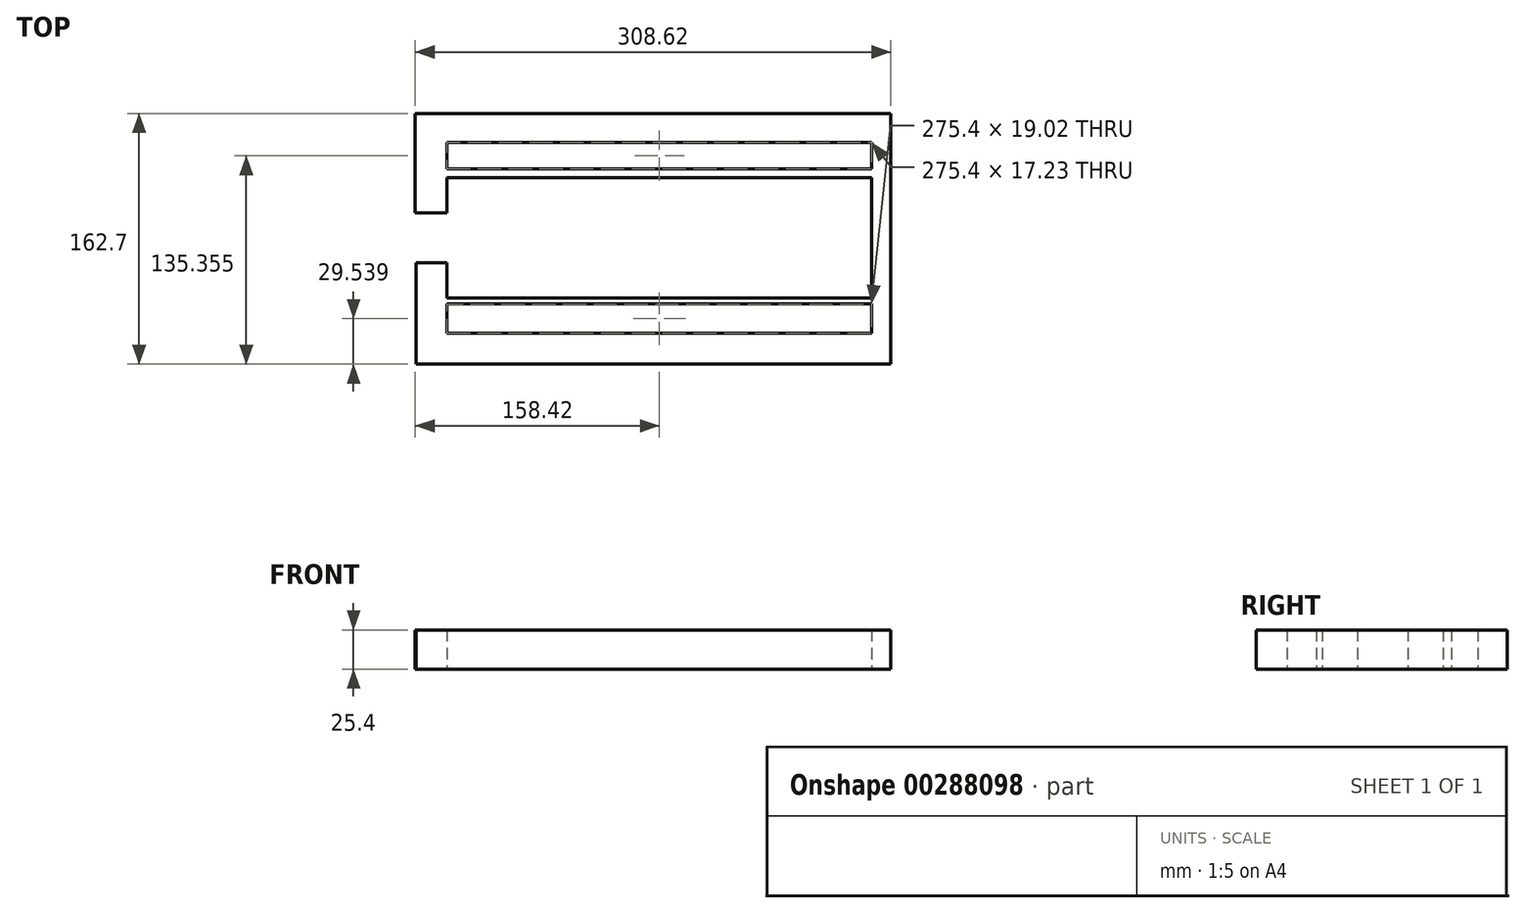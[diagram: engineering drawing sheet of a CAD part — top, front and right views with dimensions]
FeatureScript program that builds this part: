
annotation { "Feature Type Name" : "Feature", "Feature Type Description" : "" }
export const myFeature = defineFeature(function(context is Context, id is Id, definition is map)
    precondition{}
    {
        {
            var Q0;
            Q0=qCreatedBy(makeId("Top.planeOp"),FACE);
            var sketch = newSketch(context, id + "F0", { "sketchPlane" : qUnion([Q0])});
            skLineSegment(sketch, "E0.bottom", {"start": v(-152.43, -66.48) * mm, "end": v(155.5, -66.48) * mm});
            skLineSegment(sketch, "E0.top", {"start": v(-152.43, -86.51) * mm, "end": v(155.5, -86.51) * mm});
            skLineSegment(sketch, "E0.left", {"start": v(-152.43, -66.48) * mm, "end": v(-152.43, -86.51) * mm});
            skLineSegment(sketch, "E0.right", {"start": v(155.5, -66.48) * mm, "end": v(155.5, -86.51) * mm});
            skLineSegment(sketch, "E1.bottom", {"start": v(-153.12, 76.2) * mm, "end": v(155.5, 76.2) * mm});
            skLineSegment(sketch, "E1.top", {"start": v(-153.12, 57.46) * mm, "end": v(155.5, 57.46) * mm});
            skLineSegment(sketch, "E1.left", {"start": v(-153.12, 76.2) * mm, "end": v(-153.12, 57.46) * mm});
            skLineSegment(sketch, "E1.right", {"start": v(155.5, 76.2) * mm, "end": v(155.5, 57.46) * mm});
            skLineSegment(sketch, "E2", {"start": v(155.5, 57.46) * mm, "end": v(155.5, -66.48) * mm});
            skLineSegment(sketch, "E3", {"start": v(143, 57.46) * mm, "end": v(143, -66.48) * mm});
            skLineSegment(sketch, "E4", {"start": v(-153.12, 57.46) * mm, "end": v(-153.12, 37.83) * mm});
            skLineSegment(sketch, "E5", {"start": v(-152.43, -66.48) * mm, "end": v(-152.43, -20.74) * mm});
            skLineSegment(sketch, "E6", {"start": v(-153.12, 57.46) * mm, "end": v(-153.12, 11.8) * mm});
            skLineSegment(sketch, "E7", {"start": v(-132.4, 57.46) * mm, "end": v(-132.4, 11.8) * mm});
            skLineSegment(sketch, "E8", {"start": v(-153.12, 11.8) * mm, "end": v(-132.4, 11.8) * mm});
            skLineSegment(sketch, "E9", {"start": v(-132.4, -66.48) * mm, "end": v(-132.4, -20.74) * mm});
            skLineSegment(sketch, "E10", {"start": v(-152.43, -20.74) * mm, "end": v(-132.4, -20.74) * mm});
            skLineSegment(sketch, "E11", {"start": v(-132.4, -43.61) * mm, "end": v(143, -43.61) * mm});
            skLineSegment(sketch, "E12", {"start": v(-132.4, 34.63) * mm, "end": v(143, 34.63) * mm});
            skLineSegment(sketch, "E13", {"start": v(-132.4, 40.23) * mm, "end": v(143, 40.23) * mm});
            skLineSegment(sketch, "E14", {"start": v(-132.4, -61.85) * mm, "end": v(143, -61.85) * mm});
            skLineSegment(sketch, "E15", {"start": v(-132.4, -51.57) * mm, "end": v(143, -51.57) * mm});
            skLineSegment(sketch, "E16", {"start": v(-132.4, -47.46) * mm, "end": v(143, -47.46) * mm});
            skSolve(sketch);
        }
        {
            var Q0;
            Q0=makeQuery(id+"F0.imprint","IMPRINT",FACE,{"disambiguationData":[TD([[makeQuery(id+"F0.imprint","IMPRINT",EDGE,{"derivedFrom":sQuery(id+"F0.wireOp",EDGE,"E0.top")}),1.0]])]});
            extrude(context, id + "F1", {"entities" : qUnion([Q0]), "depth" : 25.4 * mm});
        }
        {
            var Q0;
            Q0 = qSketchRegion(id + "F0", true);
            extrude(context, id + "F2", {"entities" : qUnion([Q0]), "operationType" : NewBodyOperationType.ADD, "depth" : 25.4 * mm});
        }
    });
